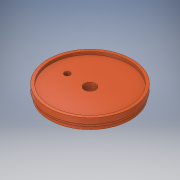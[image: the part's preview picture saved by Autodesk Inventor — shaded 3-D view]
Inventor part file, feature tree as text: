
AUTODESK INVENTOR PART (.ipt)
format: ipt  version: 2017 SP1 (Build 210196100, 196)  size: 145,920 bytes
history: native  units: in
note: dims shown in document units (in); Inventor stores cm internally (conversion verified against a paired STEP export)
features: extrude x5, sketch x5
ambient origin geometry x8: Origin, YZ Plane, XZ Plane, XY Plane, X Axis, Y Axis, Z Axis, Center Point
bodies: Solid1 (feature_tree)
feature tree (10):
  extrude  "Extrusion1"  Depth=0.25in TaperAngle=0.0deg
  extrude  "Extrusion2"  Depth=0.25in TaperAngle=0.0deg
  extrude  "Extrusion3"  Depth=0.25in TaperAngle=0.0deg
  extrude  "Extrusion4"  Depth=1.0in
  extrude  "Extrusion5"  Depth=0.25in TaperAngle=0.0deg
  sketch  "Sketch1"  dims[d0=7.15in d1=0.25in d2=0.0in]
  sketch  "Sketch2"  dims[d3=6.65in d4=0.25in d5=0.0in]
  sketch  "Sketch3"  dims[d6=7.4in d7=0.25in d8=0.0in]
  sketch  "Sketch4"  dims[d9=1.0in d10=2.0in]
  sketch  "Sketch5"  dims[d11=0.5in d12=0.25in d13=0.0in d14=7.4in d15=6.9in d16=0.25in d17=0.0in]
